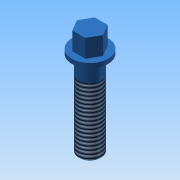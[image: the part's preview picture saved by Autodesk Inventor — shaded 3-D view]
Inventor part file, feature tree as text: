
AUTODESK INVENTOR PART (.ipt)
format: ipt  version: 2015 (Build 190159000, 159)  size: 103,424 bytes
history: native  units: mm
features: extrude x3, sketch x3, thread x1, chamfer x1
ambient origin geometry x8: Origin, YZ Plane, XZ Plane, XY Plane, X Axis, Y Axis, Z Axis, Center Point
bodies: 实体1 (feature_tree)
feature tree (8):
  extrude  "拉伸1"  Depth=1.0mm TaperAngle=0.0deg
  extrude  "拉伸2"  Depth=4.0mm TaperAngle=0.0deg
  extrude  "拉伸3"  Depth=19.0mm TaperAngle=0.0deg
  thread  "螺纹1"  [1 undecoded]
  chamfer  "倒角1"  Distance=0.25mm Angle=45.0deg
  sketch  "草图1"  dims[d0=8.0mm d1=1.0mm d2=0.0mm]
  sketch  "草图2"  dims[d3=5.0mm d4=4.0mm d5=0.0mm]
  sketch  "草图3"  dims[d6=5.0mm d7=19.0mm d8=0.0mm d9=15.0mm d10=0.0mm d11=0.25mm d12=2.0mm d13=45.0deg]
note: 1 required parameter value undecoded (feature->parameter linkage not recoverable at this tier; creation-order binding heuristic only, values carry confidence <= 0.55)
